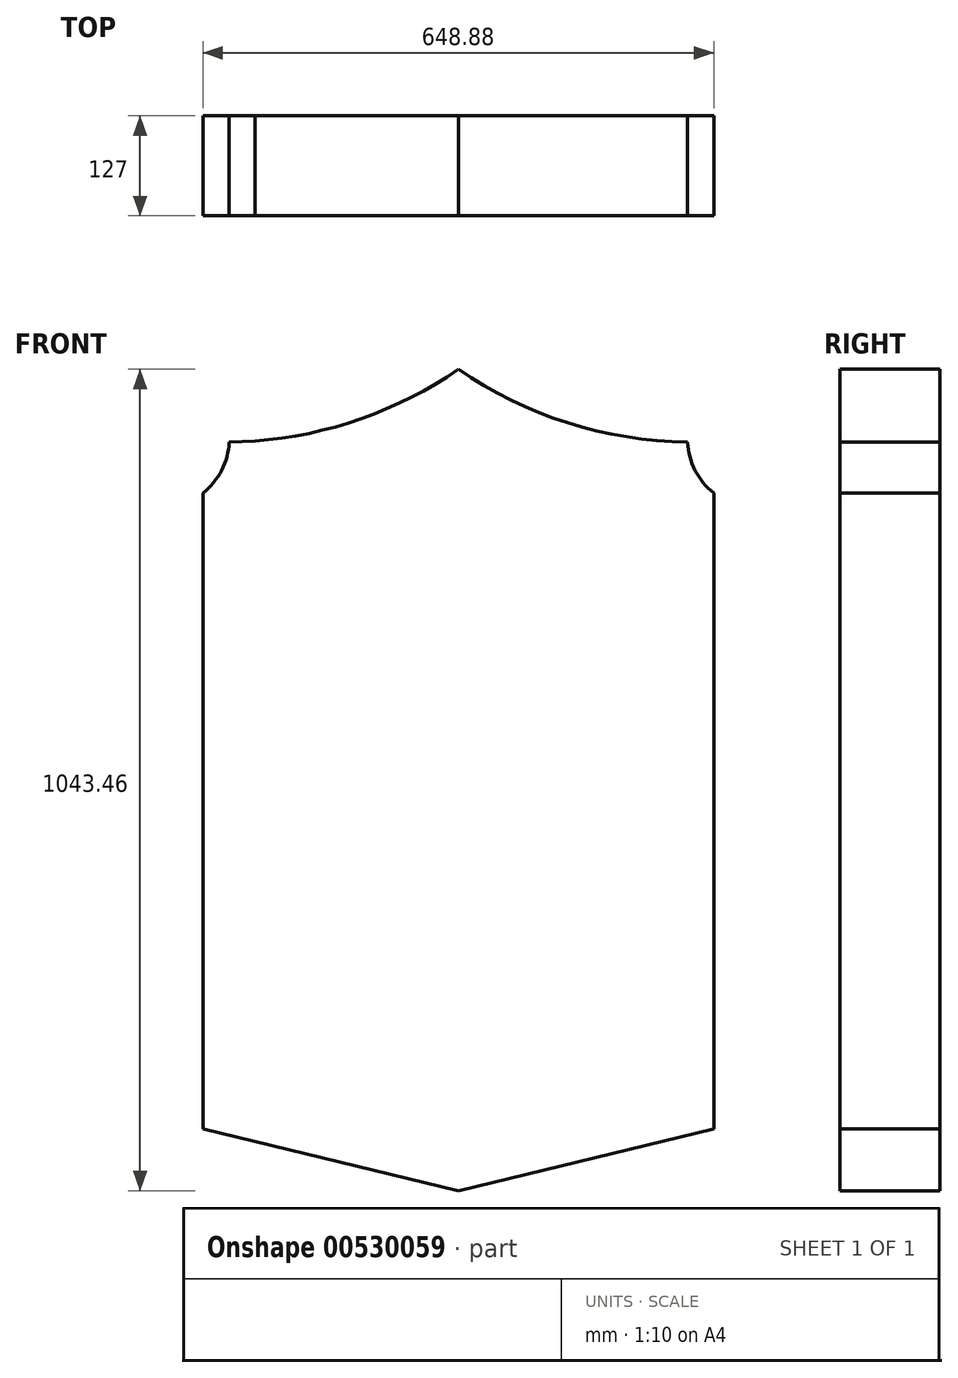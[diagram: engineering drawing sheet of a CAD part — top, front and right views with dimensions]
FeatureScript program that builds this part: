
annotation { "Feature Type Name" : "Feature", "Feature Type Description" : "" }
export const myFeature = defineFeature(function(context is Context, id is Id, definition is map)
    precondition{}
    {
        {
            var Q0;
            Q0=qCreatedBy(makeId("Front.planeOp"),FACE);
            var sketch = newSketch(context, id + "F0", { "sketchPlane" : qUnion([Q0])});
            skLineSegment(sketch, "E0.left", {"start": v(-324.44, 398.42) * mm, "end": v(-324.44, -409.12) * mm});
            skLineSegment(sketch, "E0.right", {"start": v(324.44, 398.42) * mm, "end": v(324.44, -409.12) * mm});
            skPoint(sketch, "E0.middle", {"position": v(0, 0) * mm});
            skArc(sketch, "E1", {"start": v(-270.68, 463.91) * mm, "mid": v(-128.96, 491.06) * mm, "end": v(0, 555.8) * mm});
            skArc(sketch, "E2.MirrorCS", {"start": v(291.01, 463.26) * mm, "mid": v(138.62, 487.88) * mm, "end": v(0, 555.8) * mm});
            skArc(sketch, "E3", {"start": v(291.01, 463.26) * mm, "mid": v(300.77, 427.26) * mm, "end": v(324.44, 398.42) * mm});
            skPoint(sketch, "E4.orphan", {"position": v(324.44, 463.91) * mm});
            skPoint(sketch, "E5.orphan", {"position": v(324.44, 555.8) * mm});
            skPoint(sketch, "E6.orphan", {"position": v(-324.44, 555.8) * mm});
            skPoint(sketch, "E7.orphan", {"position": v(-324.44, 463.91) * mm});
            skArc(sketch, "E8.MirrorCS", {"start": v(-291.01, 463.26) * mm, "mid": v(-300.77, 427.26) * mm, "end": v(-324.44, 398.42) * mm});
            skLineSegment(sketch, "E9", {"start": v(-291.01, 463.26) * mm, "end": v(-258.58, 464.67) * mm});
            skPoint(sketch, "E10.orphan", {"position": v(-324.44, -555.8) * mm});
            skPoint(sketch, "E11.orphan", {"position": v(324.44, -555.8) * mm});
            skLineSegment(sketch, "E12", {"start": v(-324.44, -409.12) * mm, "end": v(0, -487.66) * mm});
            skLineSegment(sketch, "E13.MirrorCS", {"start": v(324.44, -409.12) * mm, "end": v(0, -487.66) * mm});
            skPoint(sketch, "E14.end.orphan", {"position": v(-324.44, -515.98) * mm});
            skPoint(sketch, "E0.top.start.orphan", {"position": v(-228.6, -555.8) * mm});
            skPoint(sketch, "E15.MirrorCS.start.orphan", {"position": v(228.6, -555.8) * mm});
            skPoint(sketch, "E16.orphan", {"position": v(324.44, -515.98) * mm});
            skSolve(sketch);
        }
        {
            var Q0;
            Q0 = qSketchRegion(id + "F0", true);
            extrude(context, id + "F1", {"entities" : qUnion([Q0]), "depth" : 127 * mm, "offsetDistance" : 25.4 * mm});
        }
    });
